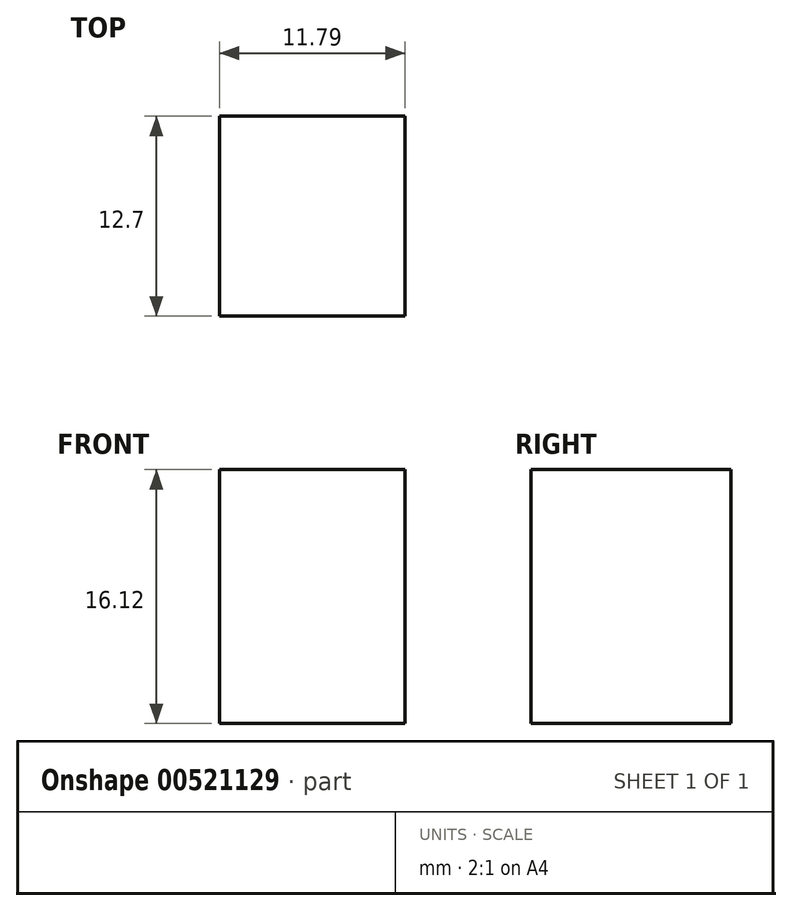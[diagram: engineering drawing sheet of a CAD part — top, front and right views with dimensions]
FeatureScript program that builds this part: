
annotation { "Feature Type Name" : "Feature", "Feature Type Description" : "" }
export const myFeature = defineFeature(function(context is Context, id is Id, definition is map)
    precondition{}
    {
        {
            var Q0;
            Q0=qCreatedBy(makeId("Front.planeOp"),FACE);
            var sketch = newSketch(context, id + "F0", { "sketchPlane" : qUnion([Q0])});
            skLineSegment(sketch, "E0", {"start": v(0, 0) * mm, "end": v(-50.93, -19.46) * mm});
            skSolve(sketch);
        }
        {
            var Q0;
            Q0=qCreatedBy(makeId("Front.planeOp"),FACE);
            var sketch = newSketch(context, id + "F1", { "sketchPlane" : qUnion([Q0])});
            skLineSegment(sketch, "E1.bottom", {"start": v(-10.93, 12.25) * mm, "end": v(-22.72, 12.25) * mm});
            skLineSegment(sketch, "E1.top", {"start": v(-10.93, 28.37) * mm, "end": v(-22.72, 28.37) * mm});
            skLineSegment(sketch, "E1.left", {"start": v(-10.93, 12.25) * mm, "end": v(-10.93, 28.37) * mm});
            skLineSegment(sketch, "E1.right", {"start": v(-22.72, 12.25) * mm, "end": v(-22.72, 28.37) * mm});
            skSolve(sketch);
        }
        {
            var Q0;
            Q0=sQuery(id+"F0.wireOp",EDGE,"E0");
            extrude(context, id + "F2", {"bodyType" : ToolBodyType.SURFACE, "surfaceEntities" : qUnion([Q0]), "depth" : 25.4 * mm, "offsetDistance" : 25.4 * mm});
        }
        {
            var Q0;
            Q0=makeQuery(id+"F1.imprint","IMPRINT",FACE,{"disambiguationData":[TD([[makeQuery(id+"F1.imprint","IMPRINT",EDGE,{"derivedFrom":sQuery(id+"F1.wireOp",EDGE,"E1.bottom")}),-1.0]])]});
            extrude(context, id + "F3", {"entities" : qUnion([Q0]), "depth" : 12.7 * mm, "offsetDistance" : 25.4 * mm});
        }
    });
